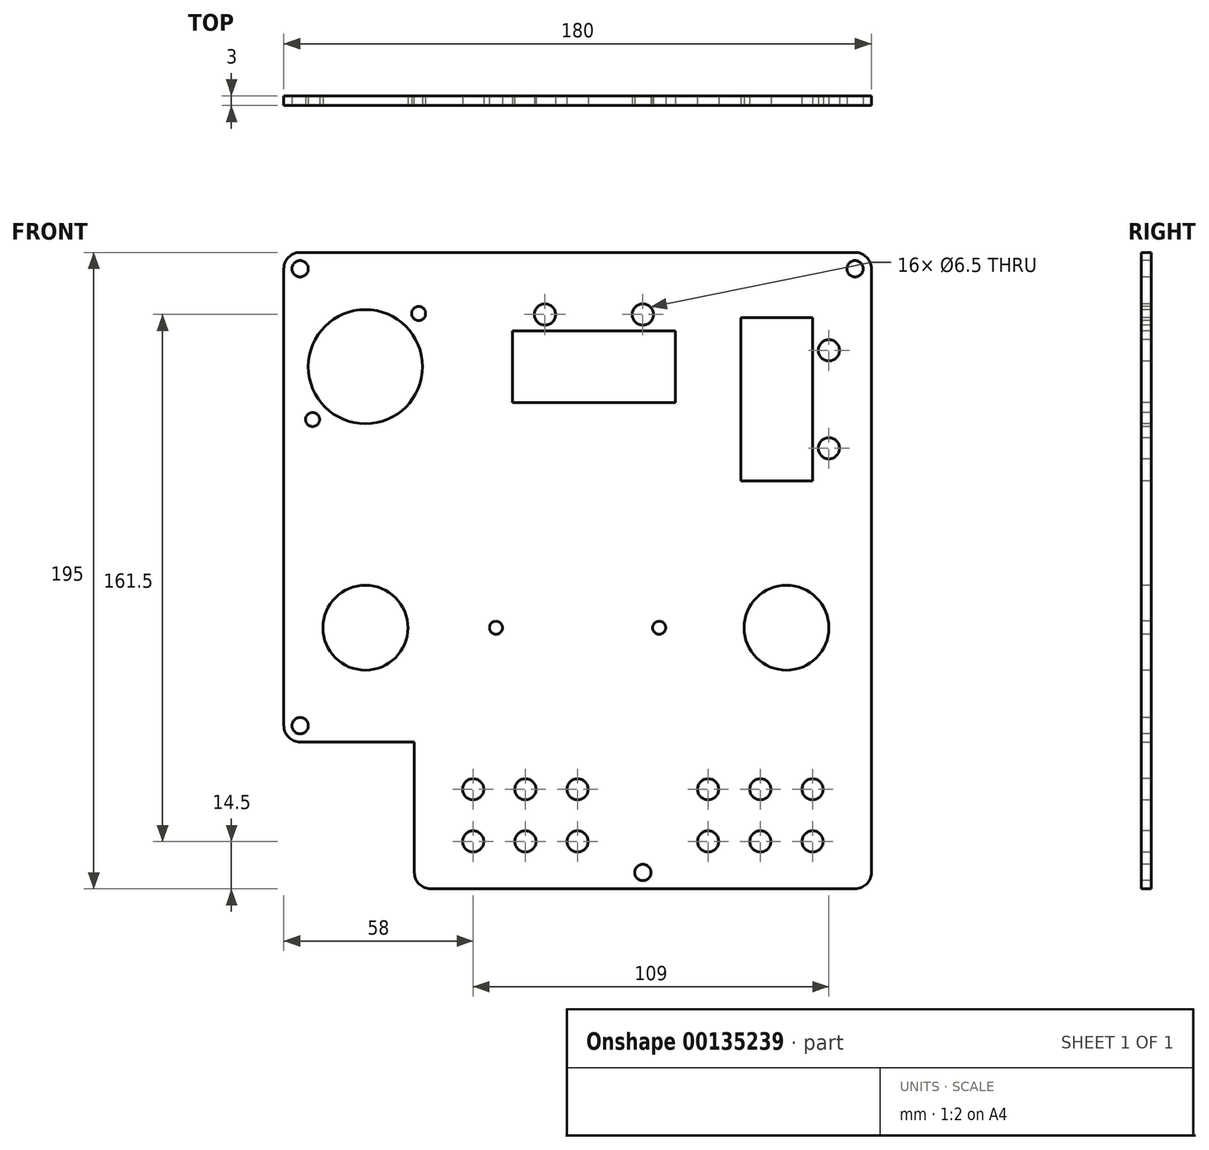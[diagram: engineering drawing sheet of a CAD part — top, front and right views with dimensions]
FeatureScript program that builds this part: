
annotation { "Feature Type Name" : "Feature", "Feature Type Description" : "" }
export const myFeature = defineFeature(function(context is Context, id is Id, definition is map)
    precondition{}
    {
        {
            var Q0;
            Q0=qCreatedBy(makeId("Front.planeOp"),FACE);
            var sketch = newSketch(context, id + "F0", { "sketchPlane" : qUnion([Q0])});
            skLineSegment(sketch, "E0.top", {"start": v(90, 75) * mm, "end": v(-90, 75) * mm});
            skLineSegment(sketch, "E0.left", {"start": v(90, -75) * mm, "end": v(90, 75) * mm});
            skLineSegment(sketch, "E0.right", {"start": v(-90, -75) * mm, "end": v(-90, 75) * mm});
            skPoint(sketch, "E0.middle", {"position": v(0, 0) * mm});
            skLineSegment(sketch, "E1", {"start": v(-90, -75) * mm, "end": v(-50, -75) * mm});
            skLineSegment(sketch, "E2", {"start": v(90, -75) * mm, "end": v(90, -120) * mm});
            skLineSegment(sketch, "E3", {"start": v(90, -120) * mm, "end": v(-50, -120) * mm});
            skLineSegment(sketch, "E4", {"start": v(-50, -120) * mm, "end": v(-50, -75) * mm});
            skSolve(sketch);
        }
        {
            var Q0;
            Q0 = qSketchRegion(id + "F0", true);
            extrude(context, id + "F1", {"entities" : qUnion([Q0]), "depth" : 3 * mm});
        }
        {
            var Q0;
            Q0=makeQuery(id+"F1.opExtrude","CAP_FACE",FACE,{"disambiguationData":[OSD([sQuery(id+"F0.wireOp",EDGE,"E0.bottom"),sQuery(id+"F0.wireOp",EDGE,"E0.top"),sQuery(id+"F0.wireOp",EDGE,"E0.left"),sQuery(id+"F0.wireOp",EDGE,"E0.right"),sQuery(id+"F0.wireOp",EDGE,"705YDGk5-Gfte-Fi4P-B9JD-DsDT6I4pTOs9"),sQuery(id+"F0.wireOp",EDGE,"xSYdZDUH-jbCC-cdi7-wa71-hGaM0zoXbeOh"),sQuery(id+"F0.wireOp",EDGE,"RaOZz3rR-saqd-X8Rh-cvnP-tlUl3yB2tA9M"),sQuery(id+"F0.wireOp",EDGE,"CzxU5fsp-Q5hC-R1Zp-2JS6-yPPf4P2xrWK5"),sQuery(id+"F0.wireOp",EDGE,"n3l6m0Ly-aGrQ-5w2v-nYG6-WW8mdSXHJLWc"),sQuery(id+"F0.wireOp",EDGE,"xjmKihOC-8ZFj-TC2J-DdJc-xlgCTcy81OrQ"),sQuery(id+"F0.wireOp",EDGE,"a61a34ca-17be-4841-85b5-a2afa722ae21.trimOffspring"),sQuery(id+"F0.wireOp",EDGE,"32e09d46-3596-48a5-a8d8-00056f8e2bac.trimOffspring")])],"isStart":false});
            var sketch = newSketch(context, id + "F2", { "sketchPlane" : qUnion([Q0])});
            skCircle(sketch, "E5", {"center": v(-65, 40) * mm, "radius": 17.5 * mm});
            skCircle(sketch, "E6", {"center": v(-65, -40) * mm, "radius": 13 * mm});
            skCircle(sketch, "E7", {"center": v(-65, 40) * mm, "radius": 23 * mm});
            skCircle(sketch, "E8", {"center": v(-48.7, 56.3) * mm, "radius": 2.15 * mm});
            skCircle(sketch, "E9", {"center": v(-81.2, 23.8) * mm, "radius": 2.15 * mm});
            skCircle(sketch, "E10", {"center": v(-25, -40) * mm, "radius": 2 * mm});
            skCircle(sketch, "E11", {"center": v(25, -40) * mm, "radius": 2 * mm});
            skCircle(sketch, "E12", {"center": v(64, -40) * mm, "radius": 13 * mm});
            skLineSegment(sketch, "E13.bottom", {"start": v(50, 55) * mm, "end": v(72, 55) * mm});
            skLineSegment(sketch, "E13.top", {"start": v(50, 5) * mm, "end": v(72, 5) * mm});
            skLineSegment(sketch, "E13.left", {"start": v(50, 55) * mm, "end": v(50, 5) * mm});
            skLineSegment(sketch, "E13.right", {"start": v(72, 55) * mm, "end": v(72, 5) * mm});
            skLineSegment(sketch, "E14.bottom", {"start": v(-20, 51) * mm, "end": v(30, 51) * mm});
            skLineSegment(sketch, "E14.top", {"start": v(-20, 29) * mm, "end": v(30, 29) * mm});
            skLineSegment(sketch, "E14.left", {"start": v(-20, 51) * mm, "end": v(-20, 29) * mm});
            skLineSegment(sketch, "E14.right", {"start": v(30, 51) * mm, "end": v(30, 29) * mm});
            skSolve(sketch);
        }
        {
            var Q0;
            Q0=makeQuery(id+"F2.imprint","IMPRINT",FACE,{"disambiguationData":[TD([[makeQuery(id+"F2.imprint","IMPRINT",EDGE,{"derivedFrom":sQuery(id+"F2.wireOp",EDGE,"E5")}),1.0]])]});
            var Q1;
            Q1=makeQuery(id+"F2.imprint","IMPRINT",FACE,{"disambiguationData":[TD([[makeQuery(id+"F2.imprint","IMPRINT",EDGE,{"derivedFrom":sQuery(id+"F2.wireOp",EDGE,"E6")}),1.0]])]});
            var Q2;
            Q2=makeQuery(id+"F2.imprint","IMPRINT",FACE,{"disambiguationData":[TD([[makeQuery(id+"F2.imprint","IMPRINT",EDGE,{"derivedFrom":sQuery(id+"F2.wireOp",EDGE,"hGJFhuIm-C7Kb-iSKH-YGYo-cKl1iigEqpWB")}),1.0]])]});
            var Q3;
            {var subQ0=sQuery(id+"F2.wireOp",EDGE,"eAQhnaM2-HMmT-E8La-HMZv-QgyqyLxRK4Xw");var subQ1=sQuery(id+"F2.wireOp",EDGE,"7H872K9c-eJwc-8Hrd-kx2C-442y8kjK0Jm9");var subQ2=makeQuery(id+"F2.imprint","INTERSECT",VERTEX,{"disambiguationData":[OD(0.0)],"derivedFrom":[subQ1,subQ0]});Q3=makeQuery(id+"F2.imprint","IMPRINT",FACE,{"disambiguationData":[TD([[makeQuery(id+"F2.imprint","IMPRINT",EDGE,{"disambiguationData":[TD([[subQ2,1.0]])],"derivedFrom":subQ1}),1.0]])]});}
            var Q4;
            {var subQ0=sQuery(id+"F2.wireOp",EDGE,"eAQhnaM2-HMmT-E8La-HMZv-QgyqyLxRK4Xw");var subQ1=sQuery(id+"F2.wireOp",EDGE,"7H872K9c-eJwc-8Hrd-kx2C-442y8kjK0Jm9");var subQ2=makeQuery(id+"F2.imprint","INTERSECT",VERTEX,{"disambiguationData":[OD(0.0)],"derivedFrom":[subQ1,subQ0]});Q4=makeQuery(id+"F2.imprint","IMPRINT",FACE,{"disambiguationData":[TD([[makeQuery(id+"F2.imprint","IMPRINT",EDGE,{"disambiguationData":[TD([[subQ2,1.0]])],"derivedFrom":subQ1}),-1.0]])]});}
            var Q5;
            {var subQ0=sQuery(id+"F2.wireOp",EDGE,"E8");var subQ1=sQuery(id+"F2.wireOp",EDGE,"E7");var subQ2=makeQuery(id+"F2.imprint","INTERSECT",VERTEX,{"disambiguationData":[OD(0.0)],"derivedFrom":[subQ1,subQ0]});Q5=makeQuery(id+"F2.imprint","IMPRINT",FACE,{"disambiguationData":[TD([[makeQuery(id+"F2.imprint","IMPRINT",EDGE,{"disambiguationData":[TD([[subQ2,1.0]])],"derivedFrom":subQ1}),-1.0]])]});}
            var Q6;
            {var subQ0=sQuery(id+"F2.wireOp",EDGE,"E8");var subQ1=sQuery(id+"F2.wireOp",EDGE,"E7");var subQ2=makeQuery(id+"F2.imprint","INTERSECT",VERTEX,{"disambiguationData":[OD(0.0)],"derivedFrom":[subQ1,subQ0]});Q6=makeQuery(id+"F2.imprint","IMPRINT",FACE,{"disambiguationData":[TD([[makeQuery(id+"F2.imprint","IMPRINT",EDGE,{"disambiguationData":[TD([[subQ2,1.0]])],"derivedFrom":subQ1}),1.0]])]});}
            var Q7;
            {var subQ0=sQuery(id+"F2.wireOp",EDGE,"E9");var subQ1=sQuery(id+"F2.wireOp",EDGE,"E7");var subQ2=makeQuery(id+"F2.imprint","INTERSECT",VERTEX,{"disambiguationData":[OD(0.0)],"derivedFrom":[subQ1,subQ0]});Q7=makeQuery(id+"F2.imprint","IMPRINT",FACE,{"disambiguationData":[TD([[makeQuery(id+"F2.imprint","IMPRINT",EDGE,{"disambiguationData":[TD([[subQ2,-1.0]])],"derivedFrom":subQ1}),1.0]])]});}
            var Q8;
            {var subQ0=sQuery(id+"F2.wireOp",EDGE,"E9");var subQ1=sQuery(id+"F2.wireOp",EDGE,"E7");var subQ2=makeQuery(id+"F2.imprint","INTERSECT",VERTEX,{"disambiguationData":[OD(0.0)],"derivedFrom":[subQ1,subQ0]});Q8=makeQuery(id+"F2.imprint","IMPRINT",FACE,{"disambiguationData":[TD([[makeQuery(id+"F2.imprint","IMPRINT",EDGE,{"disambiguationData":[TD([[subQ2,-1.0]])],"derivedFrom":subQ1}),-1.0]])]});}
            var Q9;
            {var subQ0=sQuery(id+"F2.wireOp",EDGE,"aj9FB698-IXvN-7u44-jHd2-rBrkMaW9HDzG");var subQ1=sQuery(id+"F2.wireOp",EDGE,"Ct0uPOnO-EMuZ-Bx6R-CtNH-GYaikjdUwwWW");var subQ2=makeQuery(id+"F2.imprint","INTERSECT",VERTEX,{"disambiguationData":[OD(0.0)],"derivedFrom":[subQ1,subQ0]});Q9=makeQuery(id+"F2.imprint","IMPRINT",FACE,{"disambiguationData":[TD([[makeQuery(id+"F2.imprint","IMPRINT",EDGE,{"disambiguationData":[TD([[subQ2,1.0]])],"derivedFrom":subQ1}),-1.0]])]});}
            var Q10;
            {var subQ0=sQuery(id+"F2.wireOp",EDGE,"aj9FB698-IXvN-7u44-jHd2-rBrkMaW9HDzG");var subQ1=sQuery(id+"F2.wireOp",EDGE,"Ct0uPOnO-EMuZ-Bx6R-CtNH-GYaikjdUwwWW");var subQ2=makeQuery(id+"F2.imprint","INTERSECT",VERTEX,{"disambiguationData":[OD(0.0)],"derivedFrom":[subQ1,subQ0]});Q10=makeQuery(id+"F2.imprint","IMPRINT",FACE,{"disambiguationData":[TD([[makeQuery(id+"F2.imprint","IMPRINT",EDGE,{"disambiguationData":[TD([[subQ2,1.0]])],"derivedFrom":subQ1}),1.0]])]});}
            var Q11;
            {var subQ0=sQuery(id+"F2.wireOp",EDGE,"zKlZUuii-uUpP-tPmB-f2Q8-5ALVpUUyNukW");var subQ1=sQuery(id+"F2.wireOp",EDGE,"Ct0uPOnO-EMuZ-Bx6R-CtNH-GYaikjdUwwWW");var subQ2=makeQuery(id+"F2.imprint","INTERSECT",VERTEX,{"disambiguationData":[OD(0.0)],"derivedFrom":[subQ1,subQ0]});Q11=makeQuery(id+"F2.imprint","IMPRINT",FACE,{"disambiguationData":[TD([[makeQuery(id+"F2.imprint","IMPRINT",EDGE,{"disambiguationData":[TD([[subQ2,-1.0]])],"derivedFrom":subQ1}),1.0]])]});}
            var Q12;
            {var subQ0=sQuery(id+"F2.wireOp",EDGE,"zKlZUuii-uUpP-tPmB-f2Q8-5ALVpUUyNukW");var subQ1=sQuery(id+"F2.wireOp",EDGE,"Ct0uPOnO-EMuZ-Bx6R-CtNH-GYaikjdUwwWW");var subQ2=makeQuery(id+"F2.imprint","INTERSECT",VERTEX,{"disambiguationData":[OD(0.0)],"derivedFrom":[subQ1,subQ0]});Q12=makeQuery(id+"F2.imprint","IMPRINT",FACE,{"disambiguationData":[TD([[makeQuery(id+"F2.imprint","IMPRINT",EDGE,{"disambiguationData":[TD([[subQ2,-1.0]])],"derivedFrom":subQ1}),-1.0]])]});}
            var Q13;
            {var subQ0=sQuery(id+"F2.wireOp",EDGE,"C7aO76dP-bAx2-E5EO-9tfr-QnMcRCmyayXL");var subQ1=sQuery(id+"F2.wireOp",EDGE,"7H872K9c-eJwc-8Hrd-kx2C-442y8kjK0Jm9");var subQ2=makeQuery(id+"F2.imprint","INTERSECT",VERTEX,{"disambiguationData":[OD(0.0)],"derivedFrom":[subQ1,subQ0]});Q13=makeQuery(id+"F2.imprint","IMPRINT",FACE,{"disambiguationData":[TD([[makeQuery(id+"F2.imprint","IMPRINT",EDGE,{"disambiguationData":[TD([[subQ2,-1.0]])],"derivedFrom":subQ1}),-1.0]])]});}
            var Q14;
            {var subQ0=sQuery(id+"F2.wireOp",EDGE,"C7aO76dP-bAx2-E5EO-9tfr-QnMcRCmyayXL");var subQ1=sQuery(id+"F2.wireOp",EDGE,"7H872K9c-eJwc-8Hrd-kx2C-442y8kjK0Jm9");var subQ2=makeQuery(id+"F2.imprint","INTERSECT",VERTEX,{"disambiguationData":[OD(0.0)],"derivedFrom":[subQ1,subQ0]});Q14=makeQuery(id+"F2.imprint","IMPRINT",FACE,{"disambiguationData":[TD([[makeQuery(id+"F2.imprint","IMPRINT",EDGE,{"disambiguationData":[TD([[subQ2,-1.0]])],"derivedFrom":subQ1}),1.0]])]});}
            var Q15;
            Q15=makeQuery(id+"F2.imprint","IMPRINT",FACE,{"disambiguationData":[TD([[makeQuery(id+"F2.imprint","IMPRINT",EDGE,{"derivedFrom":sQuery(id+"F2.wireOp",EDGE,"E12")}),1.0]])]});
            var Q16;
            Q16=makeQuery(id+"F2.imprint","IMPRINT",FACE,{"disambiguationData":[TD([[makeQuery(id+"F2.imprint","IMPRINT",EDGE,{"derivedFrom":sQuery(id+"F2.wireOp",EDGE,"E11")}),1.0]])]});
            var Q17;
            Q17=makeQuery(id+"F2.imprint","IMPRINT",FACE,{"disambiguationData":[TD([[makeQuery(id+"F2.imprint","IMPRINT",EDGE,{"derivedFrom":sQuery(id+"F2.wireOp",EDGE,"E10")}),1.0]])]});
            var Q18;
            Q18=makeQuery(id+"F2.imprint","IMPRINT",FACE,{"disambiguationData":[TD([[makeQuery(id+"F2.imprint","IMPRINT",EDGE,{"derivedFrom":sQuery(id+"F2.wireOp",EDGE,"E13.bottom")}),-1.0]])]});
            var Q19;
            Q19=makeQuery(id+"F2.imprint","IMPRINT",FACE,{"disambiguationData":[TD([[makeQuery(id+"F2.imprint","IMPRINT",EDGE,{"derivedFrom":sQuery(id+"F2.wireOp",EDGE,"E14.bottom")}),-1.0]])]});
            extrude(context, id + "F3", {"entities" : qUnion([Q0, Q1, Q2, Q3, Q4, Q5, Q6, Q7, Q8, Q9, Q10, Q11, Q12, Q13, Q14, Q15, Q16, Q17, Q18, Q19]), "operationType" : NewBodyOperationType.REMOVE, "endBound" : BoundingType.UP_TO_NEXT, "oppositeDirection" : true, "depth" : 25 * mm});
        }
        {
            var Q0;
            Q0=makeQuery(id+"F1.opExtrude","CAP_FACE",FACE,{"disambiguationData":[OSD([sQuery(id+"F0.wireOp",EDGE,"E0.top"),sQuery(id+"F0.wireOp",EDGE,"E0.left"),sQuery(id+"F0.wireOp",EDGE,"E0.right"),sQuery(id+"F0.wireOp",EDGE,"E1")])],"isStart":false});
            var sketch = newSketch(context, id + "F4", { "sketchPlane" : qUnion([Q0])});
            skCircle(sketch, "E15", {"center": v(-85, 70) * mm, "radius": 2.5 * mm});
            skCircle(sketch, "E16", {"center": v(85, 70) * mm, "radius": 2.5 * mm});
            skCircle(sketch, "E17", {"center": v(20, -115) * mm, "radius": 2.5 * mm});
            skCircle(sketch, "E18", {"center": v(-85, -70) * mm, "radius": 2.5 * mm});
            skSolve(sketch);
        }
        {
            var Q0;
            Q0 = qSketchRegion(id + "F4", true);
            extrude(context, id + "F5", {"entities" : qUnion([Q0]), "operationType" : NewBodyOperationType.REMOVE, "endBound" : BoundingType.UP_TO_NEXT, "oppositeDirection" : true, "depth" : 25 * mm});
        }
        {
            var Q0;
            Q0=makeQuery(id+"F1.opExtrude","CAP_FACE",FACE,{"disambiguationData":[OSD([sQuery(id+"F0.wireOp",EDGE,"E0.top"),sQuery(id+"F0.wireOp",EDGE,"E0.left"),sQuery(id+"F0.wireOp",EDGE,"E0.right"),sQuery(id+"F0.wireOp",EDGE,"E1"),sQuery(id+"F0.wireOp",EDGE,"E2"),sQuery(id+"F0.wireOp",EDGE,"E3"),sQuery(id+"F0.wireOp",EDGE,"E4")])],"isStart":false});
            var sketch = newSketch(context, id + "F6", { "sketchPlane" : qUnion([Q0])});
            skCircle(sketch, "E19", {"center": v(-32, -89.5) * mm, "radius": 3.25 * mm});
            skCircle(sketch, "E20", {"center": v(-16, -89.5) * mm, "radius": 3.25 * mm});
            skCircle(sketch, "E21", {"center": v(0, -89.5) * mm, "radius": 3.25 * mm});
            skCircle(sketch, "E22", {"center": v(40, -89.5) * mm, "radius": 3.25 * mm});
            skCircle(sketch, "E23", {"center": v(56, -89.5) * mm, "radius": 3.25 * mm});
            skCircle(sketch, "E24", {"center": v(72, -89.5) * mm, "radius": 3.25 * mm});
            skCircle(sketch, "E25", {"center": v(72, -105.5) * mm, "radius": 3.25 * mm});
            skCircle(sketch, "E26", {"center": v(56, -105.5) * mm, "radius": 3.25 * mm});
            skCircle(sketch, "E27", {"center": v(40, -105.5) * mm, "radius": 3.25 * mm});
            skCircle(sketch, "E28", {"center": v(-32, -105.5) * mm, "radius": 3.25 * mm});
            skCircle(sketch, "E29", {"center": v(-16, -105.5) * mm, "radius": 3.25 * mm});
            skCircle(sketch, "E30", {"center": v(0, -105.5) * mm, "radius": 3.25 * mm});
            skSolve(sketch);
        }
        {
            var Q0;
            Q0 = qSketchRegion(id + "F6", true);
            extrude(context, id + "F7", {"entities" : qUnion([Q0]), "operationType" : NewBodyOperationType.REMOVE, "endBound" : BoundingType.UP_TO_NEXT, "oppositeDirection" : true, "depth" : 25 * mm});
        }
        {
            var Q0;
            Q0=makeQuery(id+"F1.opExtrude","CAP_FACE",FACE,{"disambiguationData":[OSD([sQuery(id+"F0.wireOp",EDGE,"E0.top"),sQuery(id+"F0.wireOp",EDGE,"E0.left"),sQuery(id+"F0.wireOp",EDGE,"E0.right"),sQuery(id+"F0.wireOp",EDGE,"E1"),sQuery(id+"F0.wireOp",EDGE,"E2"),sQuery(id+"F0.wireOp",EDGE,"E3"),sQuery(id+"F0.wireOp",EDGE,"E4")])],"isStart":false});
            var sketch = newSketch(context, id + "F8", { "sketchPlane" : qUnion([Q0])});
            skCircle(sketch, "E31", {"center": v(-10, 56) * mm, "radius": 3.25 * mm});
            skCircle(sketch, "E32", {"center": v(20, 56) * mm, "radius": 3.25 * mm});
            skCircle(sketch, "E33", {"center": v(77, 15) * mm, "radius": 3.25 * mm});
            skCircle(sketch, "E34", {"center": v(77, 45) * mm, "radius": 3.25 * mm});
            skSolve(sketch);
        }
        {
            var Q0;
            Q0 = qSketchRegion(id + "F8", true);
            extrude(context, id + "F9", {"entities" : qUnion([Q0]), "operationType" : NewBodyOperationType.REMOVE, "endBound" : BoundingType.UP_TO_NEXT, "oppositeDirection" : true, "depth" : 25 * mm});
        }
        {
            var Q0;
            Q0=makeQuery(id+"F1.opExtrude","SWEPT_EDGE",EDGE,{"disambiguationData":[OSD([sQuery(id+"F0.wireOp",EDGE,"E0.top"),sQuery(id+"F0.wireOp",EDGE,"E0.left")])]});
            var Q1;
            Q1=makeQuery(id+"F1.opExtrude","SWEPT_EDGE",EDGE,{"disambiguationData":[OSD([sQuery(id+"F0.wireOp",EDGE,"E0.top"),sQuery(id+"F0.wireOp",EDGE,"E0.right")])]});
            var Q2;
            Q2=makeQuery(id+"F1.opExtrude","SWEPT_EDGE",EDGE,{"disambiguationData":[OSD([sQuery(id+"F0.wireOp",EDGE,"E0.right"),sQuery(id+"F0.wireOp",EDGE,"E1")])]});
            var Q3;
            Q3=makeQuery(id+"F1.opExtrude","SWEPT_EDGE",EDGE,{"disambiguationData":[OSD([sQuery(id+"F0.wireOp",EDGE,"E3"),sQuery(id+"F0.wireOp",EDGE,"E4")])]});
            var Q4;
            Q4=makeQuery(id+"F1.opExtrude","SWEPT_EDGE",EDGE,{"disambiguationData":[OSD([sQuery(id+"F0.wireOp",EDGE,"E2"),sQuery(id+"F0.wireOp",EDGE,"E3")])]});
            fillet(context, id + "F10", {"entities" : qUnion([Q0, Q1, Q2, Q3, Q4]), "radius" : 5 * mm, "tangentPropagation" : true, "allowEdgeOverflow" : false});
        }
    });
